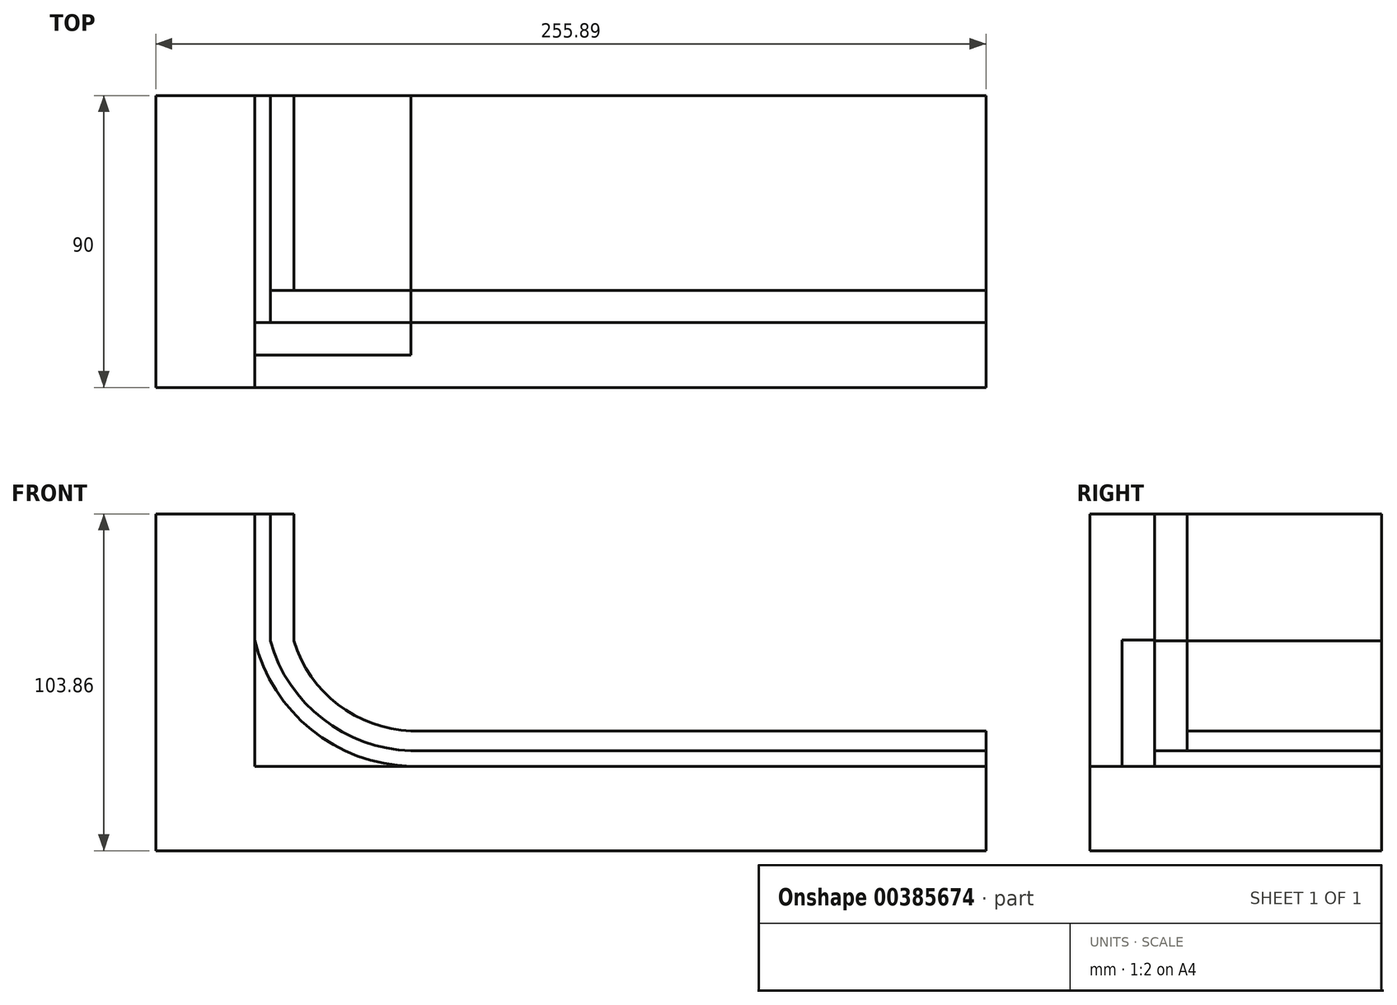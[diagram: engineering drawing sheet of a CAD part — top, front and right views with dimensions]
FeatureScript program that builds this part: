
annotation { "Feature Type Name" : "Feature", "Feature Type Description" : "" }
export const myFeature = defineFeature(function(context is Context, id is Id, definition is map)
    precondition{}
    {
        {
            var Q0;
            Q0=qCreatedBy(makeId("Front.planeOp"),FACE);
            var sketch = newSketch(context, id + "F0", { "sketchPlane" : qUnion([Q0])});
            skLineSegment(sketch, "E0", {"start": v(-144.12, 46.31) * mm, "end": v(-144.12, -57.55) * mm});
            skLineSegment(sketch, "E1", {"start": v(-144.12, -57.55) * mm, "end": v(111.77, -57.55) * mm});
            skLineSegment(sketch, "E2", {"start": v(111.77, -57.55) * mm, "end": v(111.77, -31.52) * mm});
            skLineSegment(sketch, "E3", {"start": v(111.77, -31.52) * mm, "end": v(-113.58, -31.52) * mm});
            skLineSegment(sketch, "E4", {"start": v(-113.58, -31.52) * mm, "end": v(-113.58, 46.31) * mm});
            skLineSegment(sketch, "E5", {"start": v(-113.58, 46.31) * mm, "end": v(-144.12, 46.31) * mm});
            skArc(sketch, "E6", {"start": v(-113.58, 7.4) * mm, "mid": v(-96.14, -20.25) * mm, "end": v(-65.45, -31.52) * mm});
            skLineSegment(sketch, "E7", {"start": v(-113.58, 46.31) * mm, "end": v(-108.84, 46.31) * mm});
            skLineSegment(sketch, "E8", {"start": v(-108.84, 46.31) * mm, "end": v(-108.84, 7.15) * mm});
            skArc(sketch, "E9", {"start": v(-108.84, 7.15) * mm, "mid": v(-92.7, -16.9) * mm, "end": v(-65.45, -26.72) * mm});
            skLineSegment(sketch, "E10", {"start": v(-65.45, -26.72) * mm, "end": v(111.77, -26.72) * mm});
            skLineSegment(sketch, "E11", {"start": v(111.77, -26.72) * mm, "end": v(111.77, -31.52) * mm});
            skLineSegment(sketch, "E12", {"start": v(-108.84, 46.31) * mm, "end": v(-101.56, 46.31) * mm});
            skLineSegment(sketch, "E13", {"start": v(-101.56, 46.31) * mm, "end": v(-101.56, 7.13) * mm});
            skArc(sketch, "E14", {"start": v(-101.56, 7.13) * mm, "mid": v(-87.93, -12.5) * mm, "end": v(-65.45, -20.6) * mm});
            skLineSegment(sketch, "E15", {"start": v(-65.45, -20.6) * mm, "end": v(111.77, -20.6) * mm});
            skLineSegment(sketch, "E16", {"start": v(111.77, -20.6) * mm, "end": v(111.77, -26.72) * mm});
            skSolve(sketch);
        }
        {
            var Q0;
            Q0=makeQuery(id+"F0.imprint","IMPRINT",FACE,{"disambiguationData":[TD([[makeQuery(id+"F0.imprint","IMPRINT",EDGE,{"derivedFrom":sQuery(id+"F0.wireOp",EDGE,"E0")}),1.0]])]});
            extrude(context, id + "F1", {"entities" : qUnion([Q0]), "depth" : 90 * mm});
        }
        {
            var Q0;
            {var subQ3=sQuery(id+"F0.wireOp",EDGE,"E6");Q0=makeQuery(id+"F0.imprint","IMPRINT",FACE,{"disambiguationData":[TD([[makeQuery(id+"F0.imprint","IMPRINT",EDGE,{"derivedFrom":subQ3}),-1.0]])]});}
            extrude(context, id + "F2", {"entities" : qUnion([Q0]), "depth" : 80 * mm});
        }
        {
            var Q0;
            {var subQ2=sQuery(id+"F0.wireOp",EDGE,"E6");Q0=makeQuery(id+"F0.imprint","IMPRINT",FACE,{"disambiguationData":[TD([[makeQuery(id+"F0.imprint","IMPRINT",EDGE,{"derivedFrom":subQ2}),1.0]])]});}
            extrude(context, id + "F3", {"entities" : qUnion([Q0]), "depth" : 70 * mm});
        }
        {
            var Q0;
            Q0=makeQuery(id+"F0.imprint","IMPRINT",FACE,{"disambiguationData":[TD([[makeQuery(id+"F0.imprint","IMPRINT",EDGE,{"derivedFrom":sQuery(id+"F0.wireOp",EDGE,"E8")}),1.0]])]});
            extrude(context, id + "F4", {"entities" : qUnion([Q0]), "depth" : 60 * mm});
        }
    });
